# Revit family: Shower-Shower_Trim-KOHLER-MODULO-K-78020T_1
name_source: partatom
category: Plumbing Fixtures
revit_build: Autodesk Revit 2017 (Build: 20160225_1515(x64)
units: mm (PartAtom-declared; Revit-internal decimal feet)

## family parameters
Cut with Voids When Loaded = No
Host = Face
OmniClass Number = 23.31.17.00
OmniClass Title = Showers
Part Type = Normal
Room Calculation Point = No
Round Connector Dimension = Use Diameter
Shared = No

## types (1)
- Not a Type-See Type Catalog
    ADA Compliant = No
    Assembly Code = D2010
    B4 = Yes
    B8 = No
    B9 = No
    CW Connection = Yes
    Cold Water Inlet = Cold Water Inlet
    Date Modified = 01/21/2021
    Default Elevation = 42"
    Description = Smart with wall-type rain shower valve core and panel art court rod-type handle
    Drain Included = No
    Finish = Default
    Flow Rate = 0 GPM
    HW Connection = Yes
    Handle Distance = 2 15/16"
    Height = 7 1/8"
    Hot Water Inlet = Hot Water Inlet
    Hot Water Outlet = Tempered Water Outlet
    Length = 3 7/16"
    Manufacturer = KOHLER Co.
    Master Format 2014 = 22 41 39
    Master Format 2014 Name = Residential Faucets, Supplies, and Trim
    Material = Premium Metal Construction
    Model = K-78020T-B4-CP
    Pressure = 116.03 psi
    Product Documentation Link = https://files.kohler.com.cn
    Product Name = MODULO
    Product Page URL = https://www.kohler.com.cn
    Type = 1
    URL = http://www.kohler.com.cn
    Vent Connection = No
    Waste Connection = No
    Waste Water Outlet = Waste Water Outlet
    WaterSense Certified = No
    Width = 7 1/8"

## geometry (parser evidence)
native form markers: Sweep x3
no freeform markers — native parametric forms only
